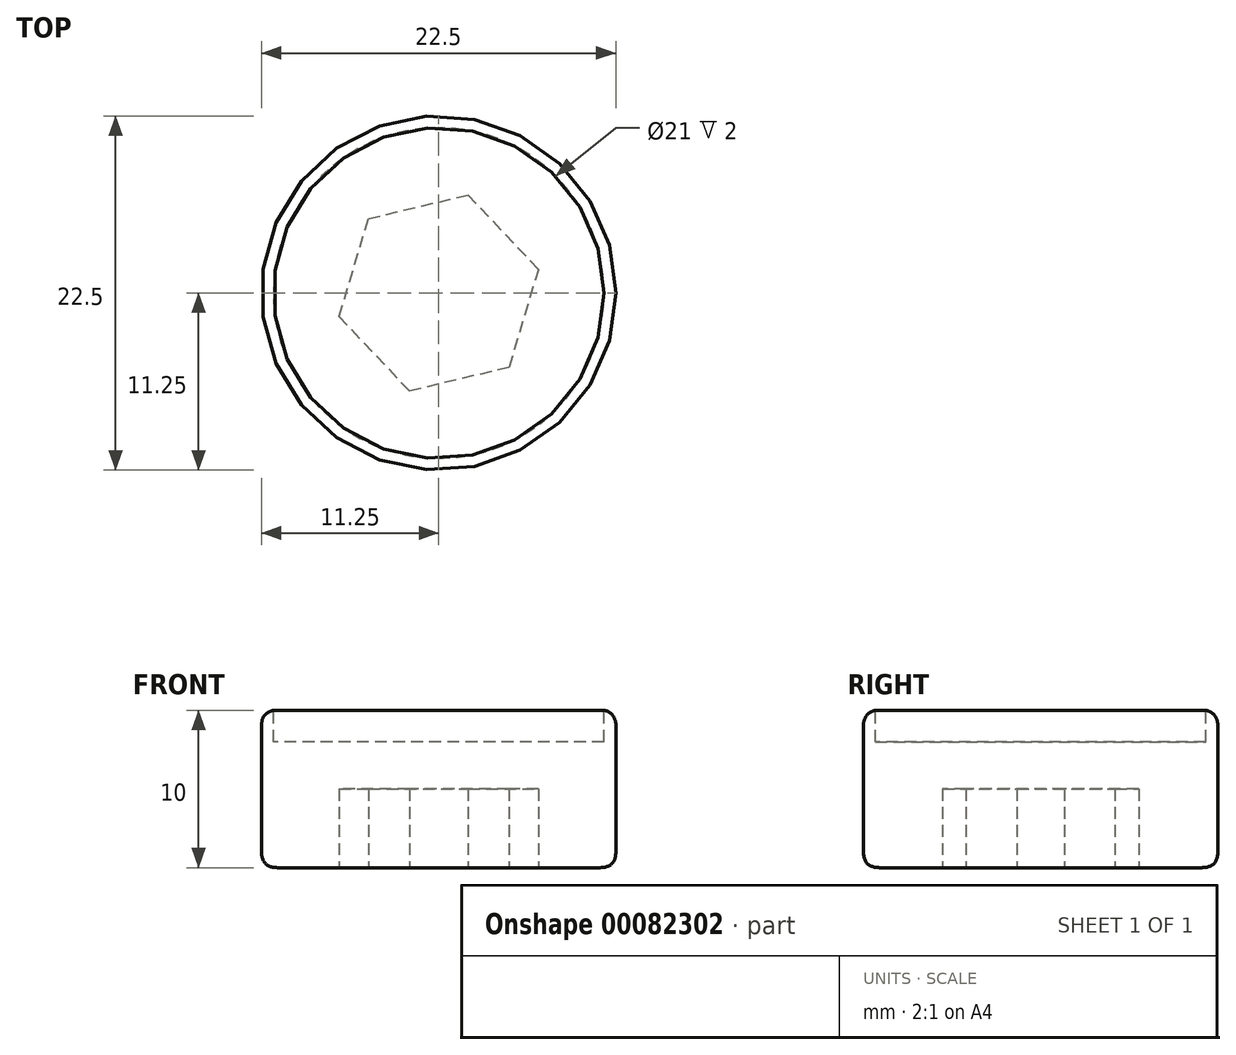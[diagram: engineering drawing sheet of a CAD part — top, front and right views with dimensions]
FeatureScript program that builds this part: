
annotation { "Feature Type Name" : "Feature", "Feature Type Description" : "" }
export const myFeature = defineFeature(function(context is Context, id is Id, definition is map)
    precondition{}
    {
        {
            var Q0;
            Q0=qCreatedBy(makeId("Top.planeOp"),FACE);
            var sketch = newSketch(context, id + "F0", { "sketchPlane" : qUnion([Q0])});
            skCircle(sketch, "E0.cCircle", {"center": v(0, 0) * mm, "radius": 6.5 * mm, "construction": true});
            skLineSegment(sketch, "E0.0", {"start": v(4.46, -4.73) * mm, "end": v(-1.86, -6.23) * mm});
            skLineSegment(sketch, "E0.1", {"start": v(-1.86, -6.23) * mm, "end": v(-6.32, -1.5) * mm});
            skLineSegment(sketch, "E0.2", {"start": v(-6.32, -1.5) * mm, "end": v(-4.46, 4.73) * mm});
            skLineSegment(sketch, "E0.3", {"start": v(-4.46, 4.73) * mm, "end": v(1.86, 6.23) * mm});
            skLineSegment(sketch, "E0.4", {"start": v(1.86, 6.23) * mm, "end": v(6.32, 1.5) * mm});
            skLineSegment(sketch, "E0.5", {"start": v(6.32, 1.5) * mm, "end": v(4.46, -4.73) * mm});
            skCircle(sketch, "E1", {"center": v(0, 0) * mm, "radius": 11.25 * mm});
            skSolve(sketch);
        }
        {
            var Q0;
            Q0=makeQuery(id+"F0.imprint","IMPRINT",FACE,{"disambiguationData":[TD([[makeQuery(id+"F0.imprint","IMPRINT",EDGE,{"derivedFrom":sQuery(id+"F0.wireOp",EDGE,"ZkOA3Flz-gcQo-jFQJ-b2dE-Bs8D0j3c0GC4")}),-1.0]])]});
            var Q1;
            Q1=makeQuery(id+"F0.imprint","IMPRINT",FACE,{"disambiguationData":[TD([[makeQuery(id+"F0.imprint","IMPRINT",EDGE,{"derivedFrom":sQuery(id+"F0.wireOp",EDGE,"E0.0")}),1.0]])]});
            var Q2;
            Q2=makeQuery(id+"F0.imprint","IMPRINT",FACE,{"disambiguationData":[TD([[makeQuery(id+"F0.imprint","IMPRINT",EDGE,{"derivedFrom":sQuery(id+"F0.wireOp",EDGE,"E0.0")}),-1.0]])]});
            extrude(context, id + "F1", {"entities" : qUnion([Q0, Q1, Q2]), "depth" : 10 * mm});
        }
        {
            var Q0;
            Q0=makeQuery(id+"F0.imprint","IMPRINT",FACE,{"disambiguationData":[TD([[makeQuery(id+"F0.imprint","IMPRINT",EDGE,{"derivedFrom":sQuery(id+"F0.wireOp",EDGE,"E0.0")}),-1.0]])]});
            extrude(context, id + "F2", {"entities" : qUnion([Q0]), "operationType" : NewBodyOperationType.REMOVE, "depth" : 5 * mm});
        }
        {
            var Q0;
            Q0=makeQuery(id+"F1.opExtrude","CAP_FACE",FACE,{"disambiguationData":[OSD([sQuery(id+"F0.wireOp",EDGE,"E1")])],"isStart":false});
            var sketch = newSketch(context, id + "F3", { "sketchPlane" : qUnion([Q0])});
            skCircle(sketch, "E2", {"center": v(0, 0) * mm, "radius": 10.5 * mm});
            skSolve(sketch);
        }
        {
            var Q0;
            Q0=makeQuery(id+"F3.imprint","IMPRINT",FACE,{"disambiguationData":[TD([[makeQuery(id+"F3.imprint","IMPRINT",EDGE,{"derivedFrom":sQuery(id+"F3.wireOp",EDGE,"E2")}),1.0]])]});
            var Q1;
            Q1=sQuery(id+"F3.wireOp",EDGE,"E2");
            extrude(context, id + "F4", {"entities" : qUnion([Q0]), "operationType" : NewBodyOperationType.REMOVE, "surfaceEntities" : qUnion([Q1]), "oppositeDirection" : true, "depth" : 2 * mm});
        }
        {
            var Q0;
            Q0=makeQuery(id+"F1.opExtrude","SWEPT_FACE",FACE,{"disambiguationData":[OSD([sQuery(id+"F0.wireOp",EDGE,"E1")])]});
            fillet(context, id + "F5", {"entities" : qUnion([Q0]), "radius" : 1 * mm, "rho" : 0.5, "crossSection" : FilletCrossSection.CONIC, "allowEdgeOverflow" : false});
        }
    });
